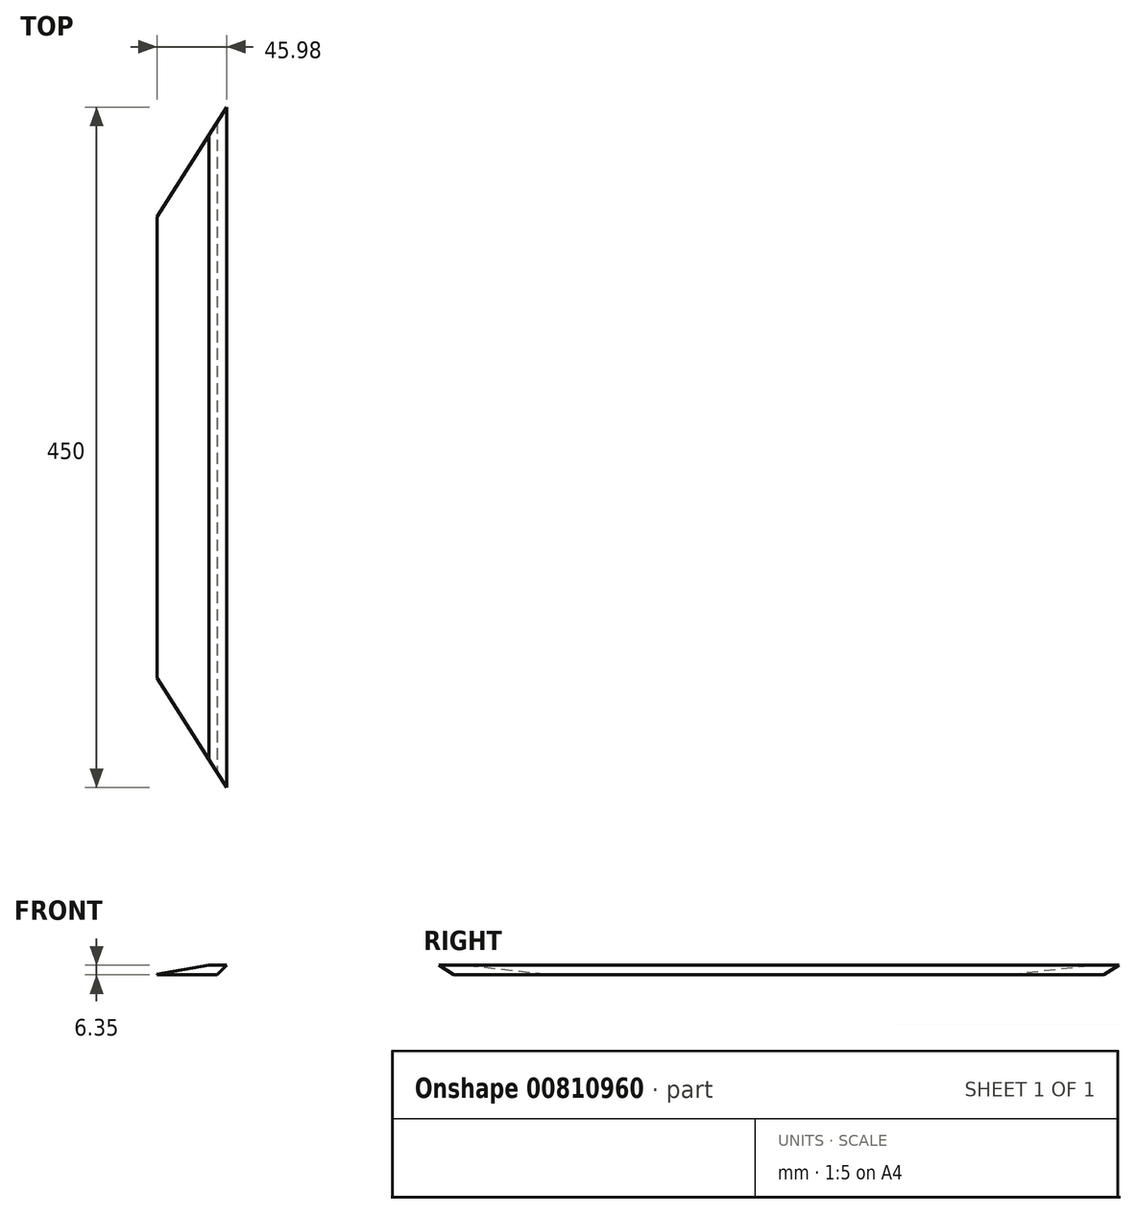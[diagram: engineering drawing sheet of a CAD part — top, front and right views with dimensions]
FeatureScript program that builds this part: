
annotation { "Feature Type Name" : "Feature", "Feature Type Description" : "" }
export const myFeature = defineFeature(function(context is Context, id is Id, definition is map)
    precondition{}
    {
        {
            var Q0;
            Q0=qCreatedBy(makeId("Top.planeOp"),FACE);
            var sketch = newSketch(context, id + "F0", { "sketchPlane" : qUnion([Q0])});
            skPoint(sketch, "E0.middle", {"position": v(0, 0) * mm});
            skLineSegment(sketch, "E1.right", {"start": v(75, 225) * mm, "end": v(75, -225) * mm});
            skLineSegment(sketch, "E2.right", {"start": v(29.02, 152.49) * mm, "end": v(29.02, -152.49) * mm});
            skLineSegment(sketch, "E3", {"start": v(29.02, 152.49) * mm, "end": v(75, 225) * mm});
            skLineSegment(sketch, "E4", {"start": v(29.02, -152.49) * mm, "end": v(75, -225) * mm});
            skSolve(sketch);
        }
        {
            var Q0;
            Q0=makeQuery(id+"F0.imprint","IMPRINT",FACE,{"disambiguationData":[TD([[makeQuery(id+"F0.imprint","IMPRINT",EDGE,{"derivedFrom":sQuery(id+"F0.wireOp",EDGE,"E1.right")}),-1.0]])]});
            extrude(context, id + "F1", {"entities" : qUnion([Q0]), "depth" : 6.35 * mm, "offsetDistance" : 25.4 * mm});
        }
        {
            var Q0;
            Q0=makeQuery(id+"F1.opExtrude","CAP_EDGE",EDGE,{"disambiguationData":[OSD([sQuery(id+"F0.wireOp",EDGE,"E1.right")])],"isStart":true});
            chamfer(context, id + "F2", {"entities" : qUnion([Q0]), "width" : 6.35 * mm});
        }
        {
            var Q0;
            Q0=makeQuery(id+"F1.opExtrude","CAP_EDGE",EDGE,{"disambiguationData":[OSD([sQuery(id+"F0.wireOp",EDGE,"E2.right")])],"isStart":false});
            chamfer(context, id + "F3", {"entities" : qUnion([Q0]), "chamferType" : ChamferType.OFFSET_ANGLE, "width" : 34.3 * mm, "oppositeDirection" : false, "angle" : 10 * degree, "tangentPropagation" : true});
        }
    });
